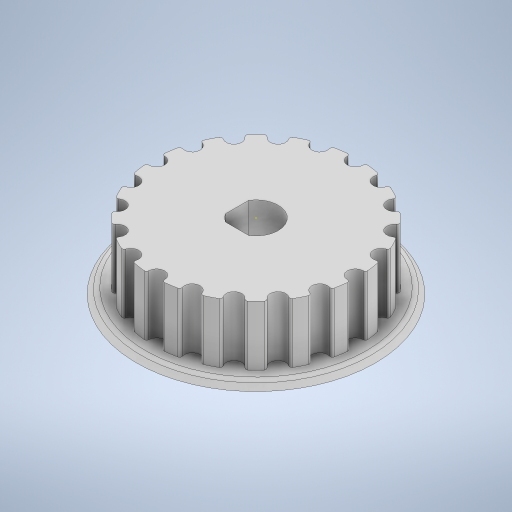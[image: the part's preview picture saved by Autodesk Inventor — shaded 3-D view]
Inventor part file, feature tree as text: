
AUTODESK INVENTOR PART (.ipt)
format: ipt  version: 2024 (Build 280153000, 153)  size: 389,120 bytes
history: native  units: mm
features: sketch x5, extrude x4, fillet x2, chamfer x1, pattern_circular x1
ambient origin geometry x8: Origin, YZ Plane, XZ Plane, XY Plane, X Axis, Y Axis, Z Axis, Center Point
bodies: Solid1 (feature_tree)
feature tree (13):
  extrude  "Extrusion1"  Depth=21.0mm TaperAngle=0.0deg
  extrude  "Extrusion2"  Depth=2.0mm
  chamfer  "Chamfer1"  Distance=2.0mm Angle=45.0deg
  fillet  "Fillet1"  Radius=2.0mm
  extrude  "Extrusion3"  Depth=6.0mm
  extrude  "Extrusion4"  Depth=5.0mm
  pattern_circular  "Circular Pattern1"  [2 undecoded]
  fillet  "Fillet2"  Radius=200.0mm
  sketch  "Sketch5"  dims[d15=31.6mm d16=19.0mm d17=0.0mm d18=200.0mm d19=360.0deg d21=0.7mm d23=6.0mm]
  sketch  "Sketch1"  dims[d0=65.0mm d1=21.0mm d2=0.0mm]
  sketch  "Sketch2"  dims[d3=2.0mm d4=0.0mm d5=76.0mm d6=2.0mm d7=2.0mm d8=45.0deg d9=2.0mm]
  sketch  "Sketch3"  dims[d10=14.1mm d11=6.0mm]
  sketch  "Sketch4"  dims[d12=40.0mm d13=0.0mm d14=5.0mm]
note: 2 required parameter values undecoded (feature->parameter linkage not recoverable at this tier; creation-order binding heuristic only, values carry confidence <= 0.55)
